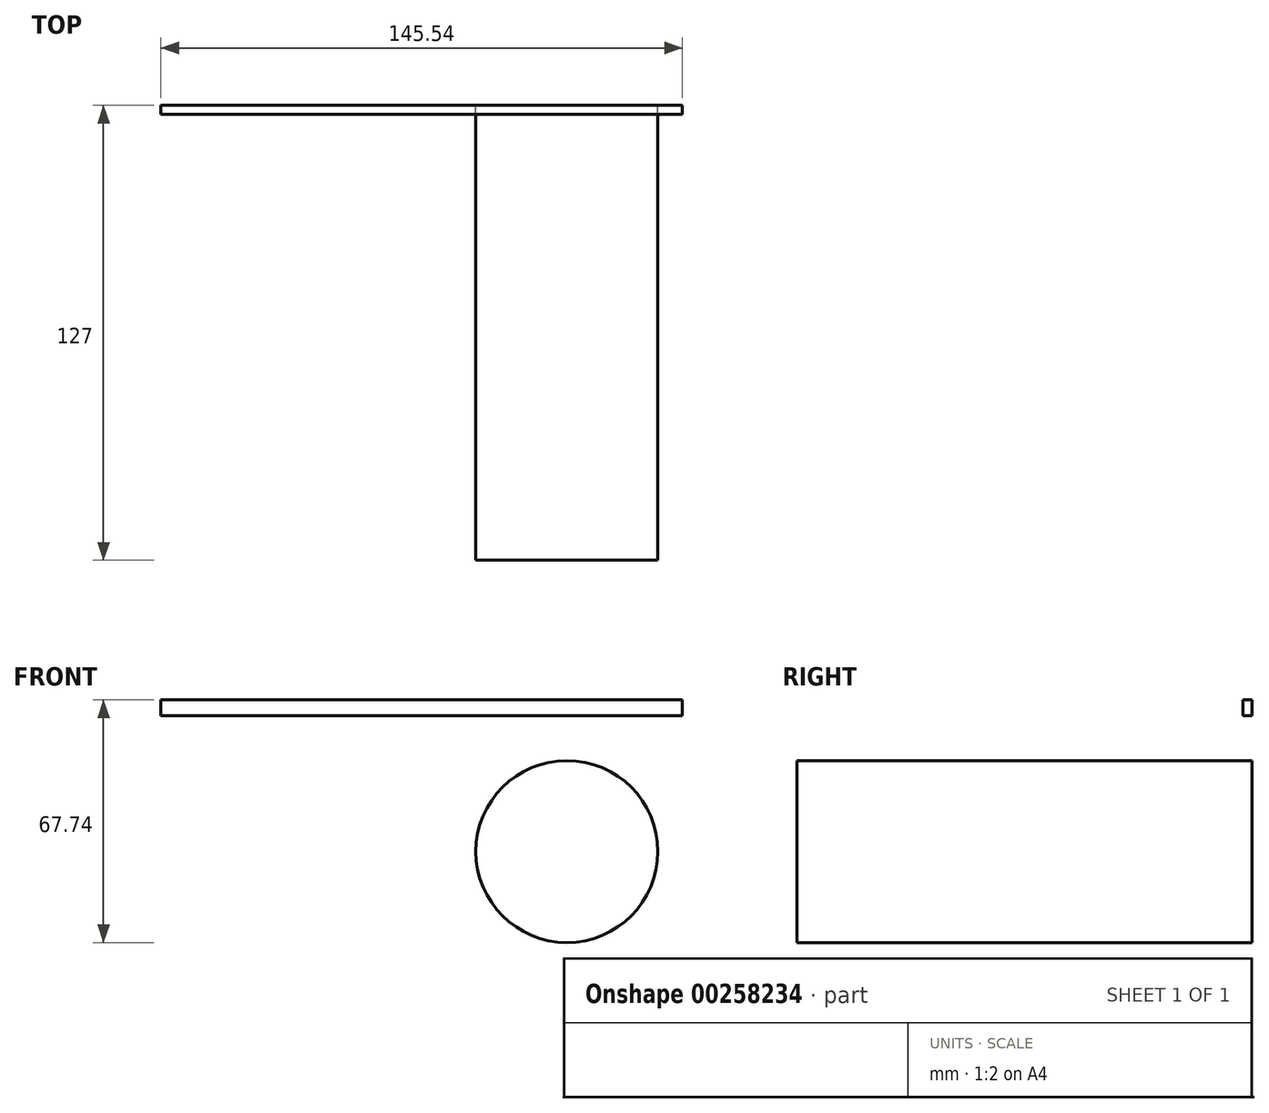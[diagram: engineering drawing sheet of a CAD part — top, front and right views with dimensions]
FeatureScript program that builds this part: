
annotation { "Feature Type Name" : "Feature", "Feature Type Description" : "" }
export const myFeature = defineFeature(function(context is Context, id is Id, definition is map)
    precondition{}
    {
        {
            var Q0;
            Q0=qCreatedBy(makeId("Front.planeOp"),FACE);
            var sketch = newSketch(context, id + "F0", { "sketchPlane" : qUnion([Q0])});
            skCircle(sketch, "E0", {"center": v(0, 0) * mm, "radius": 25.4 * mm});
            skLineSegment(sketch, "E1.bottom", {"start": v(32.24, 42.34) * mm, "end": v(-113.3, 42.34) * mm});
            skLineSegment(sketch, "E1.top", {"start": v(32.24, 37.94) * mm, "end": v(-113.3, 37.94) * mm});
            skLineSegment(sketch, "E1.left", {"start": v(32.24, 42.34) * mm, "end": v(32.24, 37.94) * mm});
            skLineSegment(sketch, "E1.right", {"start": v(-113.3, 42.34) * mm, "end": v(-113.3, 37.94) * mm});
            skPoint(sketch, "E1.middle", {"position": v(-40.53, 40.14) * mm});
            skSolve(sketch);
        }
        {
            var Q0;
            Q0=makeQuery(id+"F0.imprint","IMPRINT",FACE,{"disambiguationData":[TD([[makeQuery(id+"F0.imprint","IMPRINT",EDGE,{"derivedFrom":sQuery(id+"F0.wireOp",EDGE,"E1.bottom")}),1.0]])]});
            extrude(context, id + "F1", {"entities" : qUnion([Q0]), "depth" : 2.54 * mm});
        }
        {
            var Q0;
            Q0=makeQuery(id+"F0.imprint","IMPRINT",FACE,{"disambiguationData":[TD([[makeQuery(id+"F0.imprint","IMPRINT",EDGE,{"derivedFrom":sQuery(id+"F0.wireOp",EDGE,"E0")}),1.0]])]});
            extrude(context, id + "F2", {"entities" : qUnion([Q0]), "depth" : 127 * mm});
        }
    });
